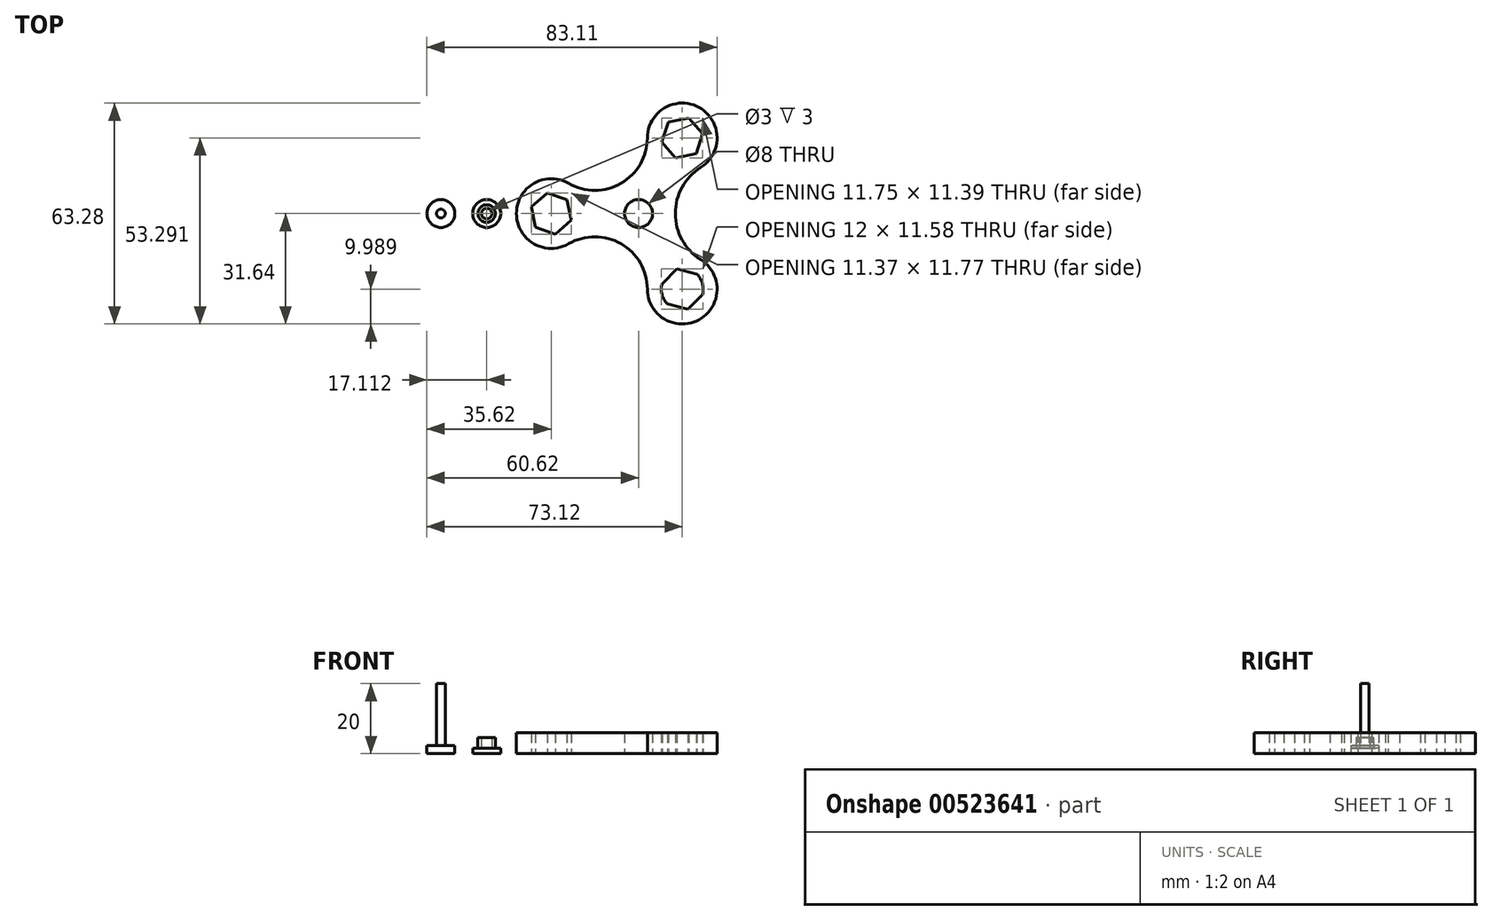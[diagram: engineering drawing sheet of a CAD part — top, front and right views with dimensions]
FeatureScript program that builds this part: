
annotation { "Feature Type Name" : "Feature", "Feature Type Description" : "" }
export const myFeature = defineFeature(function(context is Context, id is Id, definition is map)
    precondition{}
    {
        {
            var Q0;
            Q0=qCreatedBy(makeId("Top.planeOp"),FACE);
            var sketch = newSketch(context, id + "F0", { "sketchPlane" : qUnion([Q0])});
            skCircle(sketch, "E0", {"center": v(0, 0) * mm, "radius": 25 * mm});
            skCircle(sketch, "E1", {"center": v(-25, 0) * mm, "radius": 9.99 * mm});
            skCircle(sketch, "E2.2.1", {"center": v(12.5, -21.65) * mm, "radius": 9.99 * mm});
            skCircle(sketch, "E2.4.1", {"center": v(12.5, 21.65) * mm, "radius": 9.99 * mm});
            skCircle(sketch, "E3.cCircle", {"center": v(12.5, -21.65) * mm, "radius": 6 * mm, "construction": true});
            skLineSegment(sketch, "E3.0", {"start": v(8.28, -25.91) * mm, "end": v(6.7, -20.12) * mm});
            skLineSegment(sketch, "E3.1", {"start": v(6.7, -20.12) * mm, "end": v(10.92, -15.86) * mm});
            skLineSegment(sketch, "E3.2", {"start": v(10.92, -15.86) * mm, "end": v(16.72, -17.4) * mm});
            skLineSegment(sketch, "E3.3", {"start": v(16.72, -17.4) * mm, "end": v(18.3, -23.18) * mm});
            skLineSegment(sketch, "E3.4", {"start": v(18.3, -23.18) * mm, "end": v(14.08, -27.44) * mm});
            skLineSegment(sketch, "E3.5", {"start": v(14.08, -27.44) * mm, "end": v(8.28, -25.91) * mm});
            skCircle(sketch, "E4", {"center": v(12.5, -21.65) * mm, "radius": 6 * mm});
            skCircle(sketch, "E5", {"center": v(12.5, 21.65) * mm, "radius": 6 * mm});
            skCircle(sketch, "E6", {"center": v(-25, 0) * mm, "radius": 6 * mm});
            skCircle(sketch, "E7.cCircle", {"center": v(-25, 0) * mm, "radius": 6 * mm, "construction": true});
            skLineSegment(sketch, "E7.0", {"start": v(-29.5, -3.96) * mm, "end": v(-30.68, 1.92) * mm});
            skLineSegment(sketch, "E7.1", {"start": v(-30.68, 1.92) * mm, "end": v(-26.18, 5.88) * mm});
            skLineSegment(sketch, "E7.2", {"start": v(-26.18, 5.88) * mm, "end": v(-20.5, 3.96) * mm});
            skLineSegment(sketch, "E7.3", {"start": v(-20.5, 3.96) * mm, "end": v(-19.32, -1.92) * mm});
            skLineSegment(sketch, "E7.4", {"start": v(-19.32, -1.92) * mm, "end": v(-23.82, -5.88) * mm});
            skLineSegment(sketch, "E7.5", {"start": v(-23.82, -5.88) * mm, "end": v(-29.5, -3.96) * mm});
            skCircle(sketch, "E8.cCircle", {"center": v(12.5, 21.65) * mm, "radius": 6 * mm, "construction": true});
            skLineSegment(sketch, "E8.0", {"start": v(6.62, 20.44) * mm, "end": v(8.52, 26.14) * mm});
            skLineSegment(sketch, "E8.1", {"start": v(8.52, 26.14) * mm, "end": v(14.4, 27.34) * mm});
            skLineSegment(sketch, "E8.2", {"start": v(14.4, 27.34) * mm, "end": v(18.38, 22.86) * mm});
            skLineSegment(sketch, "E8.3", {"start": v(18.38, 22.86) * mm, "end": v(16.48, 17.16) * mm});
            skLineSegment(sketch, "E8.4", {"start": v(16.48, 17.16) * mm, "end": v(10.6, 15.96) * mm});
            skLineSegment(sketch, "E8.5", {"start": v(10.6, 15.96) * mm, "end": v(6.62, 20.44) * mm});
            skArc(sketch, "E9", {"start": v(2.15, -24.9) * mm, "mid": v(-5, -8.65) * mm, "end": v(-22.65, -10.59) * mm});
            skArc(sketch, "E10", {"start": v(-22.65, 10.59) * mm, "mid": v(-5, 8.65) * mm, "end": v(2.15, 24.9) * mm});
            skArc(sketch, "E11", {"start": v(20.38, 14.49) * mm, "mid": v(10.51, 0) * mm, "end": v(20.38, -14.49) * mm});
            skPoint(sketch, "E2.3.1.center.orphan", {"position": v(25, 0) * mm});
            skCircle(sketch, "E12", {"center": v(0, 0) * mm, "radius": 4 * mm});
            skSolve(sketch);
        }
        {
            var Q0;
            {var subQ1=sQuery(id+"F0.wireOp",EDGE,"E1");var subQ8=sQuery(id+"F0.wireOp",EDGE,"E10");var subQ10=makeQuery(id+"F0.imprint","INTERSECT",VERTEX,{"derivedFrom":[subQ1,subQ8]});Q0=makeQuery(id+"F0.imprint","IMPRINT",FACE,{"disambiguationData":[TD([[makeQuery(id+"F0.imprint","IMPRINT",EDGE,{"disambiguationData":[TD([[subQ10,1.0]])],"derivedFrom":subQ1}),-1.0]])]});}
            var Q1;
            {var subQ0=sQuery(id+"F0.wireOp",EDGE,"E1");var subQ3=sQuery(id+"F0.wireOp",EDGE,"E0");var subQ4=makeQuery(id+"F0.imprint","INTERSECT",VERTEX,{"disambiguationData":[OD(0.0)],"derivedFrom":[subQ0,subQ3]});Q1=makeQuery(id+"F0.imprint","IMPRINT",FACE,{"disambiguationData":[TD([[makeQuery(id+"F0.imprint","IMPRINT",EDGE,{"disambiguationData":[TD([[subQ4,1.0]])],"derivedFrom":subQ0}),1.0]])]});}
            var Q2;
            {var subQ0=sQuery(id+"F0.wireOp",EDGE,"E0");var subQ1=sQuery(id+"F0.wireOp",EDGE,"E1");var subQ9=makeQuery(id+"F0.imprint","INTERSECT",VERTEX,{"disambiguationData":[OD(0.0)],"derivedFrom":[subQ1,subQ0]});Q2=makeQuery(id+"F0.imprint","IMPRINT",FACE,{"disambiguationData":[TD([[makeQuery(id+"F0.imprint","IMPRINT",EDGE,{"disambiguationData":[TD([[subQ9,-1.0]])],"derivedFrom":subQ1}),1.0]])]});}
            var Q3;
            {var subQ0=sQuery(id+"F0.wireOp",EDGE,"E7.1");Q3=makeQuery(id+"F0.imprint","IMPRINT",FACE,{"disambiguationData":[TD([[makeQuery(id+"F0.imprint","IMPRINT",EDGE,{"derivedFrom":subQ0}),1.0]])]});}
            var Q4;
            {var subQ0=sQuery(id+"F0.wireOp",EDGE,"E7.0");Q4=makeQuery(id+"F0.imprint","IMPRINT",FACE,{"disambiguationData":[TD([[makeQuery(id+"F0.imprint","IMPRINT",EDGE,{"derivedFrom":subQ0}),1.0]])]});}
            var Q5;
            {var subQ0=sQuery(id+"F0.wireOp",EDGE,"E7.5");var subQ1=sQuery(id+"F0.wireOp",EDGE,"E0");var subQ2=makeQuery(id+"F0.imprint","INTERSECT",VERTEX,{"derivedFrom":[subQ1,subQ0]});Q5=makeQuery(id+"F0.imprint","IMPRINT",FACE,{"disambiguationData":[TD([[makeQuery(id+"F0.imprint","IMPRINT",EDGE,{"disambiguationData":[TD([[subQ2,-1.0]])],"derivedFrom":subQ1}),-1.0]])]});}
            var Q6;
            {var subQ0=sQuery(id+"F0.wireOp",EDGE,"E7.4");Q6=makeQuery(id+"F0.imprint","IMPRINT",FACE,{"disambiguationData":[TD([[makeQuery(id+"F0.imprint","IMPRINT",EDGE,{"derivedFrom":subQ0}),1.0]])]});}
            var Q7;
            {var subQ0=sQuery(id+"F0.wireOp",EDGE,"E7.3");Q7=makeQuery(id+"F0.imprint","IMPRINT",FACE,{"disambiguationData":[TD([[makeQuery(id+"F0.imprint","IMPRINT",EDGE,{"derivedFrom":subQ0}),1.0]])]});}
            var Q8;
            {var subQ0=sQuery(id+"F0.wireOp",EDGE,"E6");var subQ1=sQuery(id+"F0.wireOp",EDGE,"E0");var subQ2=makeQuery(id+"F0.imprint","INTERSECT",VERTEX,{"disambiguationData":[OD(0.0)],"derivedFrom":[subQ1,subQ0]});Q8=makeQuery(id+"F0.imprint","IMPRINT",FACE,{"disambiguationData":[TD([[makeQuery(id+"F0.imprint","IMPRINT",EDGE,{"disambiguationData":[TD([[subQ2,-1.0]])],"derivedFrom":subQ1}),1.0]])]});}
            var Q9;
            {var subQ0=sQuery(id+"F0.wireOp",EDGE,"E0");var subQ1=sQuery(id+"F0.wireOp",EDGE,"E2.2.1");var subQ11=makeQuery(id+"F0.imprint","INTERSECT",VERTEX,{"disambiguationData":[OD(0.0)],"derivedFrom":[subQ1,subQ0]});Q9=makeQuery(id+"F0.imprint","IMPRINT",FACE,{"disambiguationData":[TD([[makeQuery(id+"F0.imprint","IMPRINT",EDGE,{"disambiguationData":[TD([[subQ11,1.0]])],"derivedFrom":subQ1}),1.0]])]});}
            var Q10;
            {var subQ3=sQuery(id+"F0.wireOp",EDGE,"E0");var subQ5=sQuery(id+"F0.wireOp",EDGE,"E2.2.1");var subQ6=makeQuery(id+"F0.imprint","INTERSECT",VERTEX,{"disambiguationData":[OD(0.0)],"derivedFrom":[subQ5,subQ3]});Q10=makeQuery(id+"F0.imprint","IMPRINT",FACE,{"disambiguationData":[TD([[makeQuery(id+"F0.imprint","IMPRINT",EDGE,{"disambiguationData":[TD([[subQ6,-1.0]])],"derivedFrom":subQ5}),1.0]])]});}
            var Q11;
            {var subQ0=sQuery(id+"F0.wireOp",EDGE,"E3.4");Q11=makeQuery(id+"F0.imprint","IMPRINT",FACE,{"disambiguationData":[TD([[makeQuery(id+"F0.imprint","IMPRINT",EDGE,{"derivedFrom":subQ0}),1.0]])]});}
            var Q12;
            {var subQ0=sQuery(id+"F0.wireOp",EDGE,"E3.5");Q12=makeQuery(id+"F0.imprint","IMPRINT",FACE,{"disambiguationData":[TD([[makeQuery(id+"F0.imprint","IMPRINT",EDGE,{"derivedFrom":subQ0}),1.0]])]});}
            var Q13;
            {var subQ0=sQuery(id+"F0.wireOp",EDGE,"E4");var subQ1=sQuery(id+"F0.wireOp",EDGE,"E0");var subQ2=makeQuery(id+"F0.imprint","INTERSECT",VERTEX,{"disambiguationData":[OD(1.0)],"derivedFrom":[subQ1,subQ0]});Q13=makeQuery(id+"F0.imprint","IMPRINT",FACE,{"disambiguationData":[TD([[makeQuery(id+"F0.imprint","IMPRINT",EDGE,{"disambiguationData":[TD([[subQ2,-1.0]])],"derivedFrom":subQ1}),1.0]])]});}
            var Q14;
            {var subQ0=sQuery(id+"F0.wireOp",EDGE,"E4");var subQ1=sQuery(id+"F0.wireOp",EDGE,"E0");var subQ2=makeQuery(id+"F0.imprint","INTERSECT",VERTEX,{"disambiguationData":[OD(1.0)],"derivedFrom":[subQ1,subQ0]});Q14=makeQuery(id+"F0.imprint","IMPRINT",FACE,{"disambiguationData":[TD([[makeQuery(id+"F0.imprint","IMPRINT",EDGE,{"disambiguationData":[TD([[subQ2,-1.0]])],"derivedFrom":subQ1}),-1.0]])]});}
            var Q15;
            {var subQ0=sQuery(id+"F0.wireOp",EDGE,"E3.1");Q15=makeQuery(id+"F0.imprint","IMPRINT",FACE,{"disambiguationData":[TD([[makeQuery(id+"F0.imprint","IMPRINT",EDGE,{"derivedFrom":subQ0}),1.0]])]});}
            var Q16;
            {var subQ0=sQuery(id+"F0.wireOp",EDGE,"E3.2");Q16=makeQuery(id+"F0.imprint","IMPRINT",FACE,{"disambiguationData":[TD([[makeQuery(id+"F0.imprint","IMPRINT",EDGE,{"derivedFrom":subQ0}),1.0]])]});}
            var Q17;
            {var subQ0=sQuery(id+"F0.wireOp",EDGE,"E4");var subQ1=sQuery(id+"F0.wireOp",EDGE,"E0");var subQ2=makeQuery(id+"F0.imprint","INTERSECT",VERTEX,{"disambiguationData":[OD(0.0)],"derivedFrom":[subQ1,subQ0]});Q17=makeQuery(id+"F0.imprint","IMPRINT",FACE,{"disambiguationData":[TD([[makeQuery(id+"F0.imprint","IMPRINT",EDGE,{"disambiguationData":[TD([[subQ2,1.0]])],"derivedFrom":subQ1}),-1.0]])]});}
            var Q18;
            {var subQ0=sQuery(id+"F0.wireOp",EDGE,"E4");var subQ1=sQuery(id+"F0.wireOp",EDGE,"E0");var subQ2=makeQuery(id+"F0.imprint","INTERSECT",VERTEX,{"disambiguationData":[OD(0.0)],"derivedFrom":[subQ1,subQ0]});Q18=makeQuery(id+"F0.imprint","IMPRINT",FACE,{"disambiguationData":[TD([[makeQuery(id+"F0.imprint","IMPRINT",EDGE,{"disambiguationData":[TD([[subQ2,1.0]])],"derivedFrom":subQ1}),1.0]])]});}
            var Q19;
            {var subQ0=sQuery(id+"F0.wireOp",EDGE,"E0");var subQ1=sQuery(id+"F0.wireOp",EDGE,"E2.4.1");var subQ2=makeQuery(id+"F0.imprint","INTERSECT",VERTEX,{"disambiguationData":[OD(0.0)],"derivedFrom":[subQ1,subQ0]});Q19=makeQuery(id+"F0.imprint","IMPRINT",FACE,{"disambiguationData":[TD([[makeQuery(id+"F0.imprint","IMPRINT",EDGE,{"disambiguationData":[TD([[subQ2,1.0]])],"derivedFrom":subQ1}),1.0]])]});}
            var Q20;
            {var subQ0=sQuery(id+"F0.wireOp",EDGE,"E0");var subQ1=sQuery(id+"F0.wireOp",EDGE,"E2.4.1");var subQ10=makeQuery(id+"F0.imprint","INTERSECT",VERTEX,{"disambiguationData":[OD(0.0)],"derivedFrom":[subQ1,subQ0]});Q20=makeQuery(id+"F0.imprint","IMPRINT",FACE,{"disambiguationData":[TD([[makeQuery(id+"F0.imprint","IMPRINT",EDGE,{"disambiguationData":[TD([[subQ10,-1.0]])],"derivedFrom":subQ1}),1.0]])]});}
            var Q21;
            {var subQ0=sQuery(id+"F0.wireOp",EDGE,"E8.5");Q21=makeQuery(id+"F0.imprint","IMPRINT",FACE,{"disambiguationData":[TD([[makeQuery(id+"F0.imprint","IMPRINT",EDGE,{"derivedFrom":subQ0}),1.0]])]});}
            var Q22;
            {var subQ0=sQuery(id+"F0.wireOp",EDGE,"E8.0");var subQ1=sQuery(id+"F0.wireOp",EDGE,"E0");var subQ2=makeQuery(id+"F0.imprint","INTERSECT",VERTEX,{"derivedFrom":[subQ1,subQ0]});Q22=makeQuery(id+"F0.imprint","IMPRINT",FACE,{"disambiguationData":[TD([[makeQuery(id+"F0.imprint","IMPRINT",EDGE,{"disambiguationData":[TD([[subQ2,-1.0]])],"derivedFrom":subQ1}),1.0]])]});}
            var Q23;
            {var subQ0=sQuery(id+"F0.wireOp",EDGE,"E8.0");var subQ1=sQuery(id+"F0.wireOp",EDGE,"E0");var subQ2=makeQuery(id+"F0.imprint","INTERSECT",VERTEX,{"derivedFrom":[subQ1,subQ0]});Q23=makeQuery(id+"F0.imprint","IMPRINT",FACE,{"disambiguationData":[TD([[makeQuery(id+"F0.imprint","IMPRINT",EDGE,{"disambiguationData":[TD([[subQ2,-1.0]])],"derivedFrom":subQ1}),-1.0]])]});}
            var Q24;
            {var subQ0=sQuery(id+"F0.wireOp",EDGE,"E8.1");Q24=makeQuery(id+"F0.imprint","IMPRINT",FACE,{"disambiguationData":[TD([[makeQuery(id+"F0.imprint","IMPRINT",EDGE,{"derivedFrom":subQ0}),1.0]])]});}
            var Q25;
            {var subQ0=sQuery(id+"F0.wireOp",EDGE,"E8.2");Q25=makeQuery(id+"F0.imprint","IMPRINT",FACE,{"disambiguationData":[TD([[makeQuery(id+"F0.imprint","IMPRINT",EDGE,{"derivedFrom":subQ0}),1.0]])]});}
            var Q26;
            {var subQ0=sQuery(id+"F0.wireOp",EDGE,"E5");var subQ1=sQuery(id+"F0.wireOp",EDGE,"E0");var subQ2=makeQuery(id+"F0.imprint","INTERSECT",VERTEX,{"disambiguationData":[OD(0.0)],"derivedFrom":[subQ1,subQ0]});Q26=makeQuery(id+"F0.imprint","IMPRINT",FACE,{"disambiguationData":[TD([[makeQuery(id+"F0.imprint","IMPRINT",EDGE,{"disambiguationData":[TD([[subQ2,-1.0]])],"derivedFrom":subQ1}),-1.0]])]});}
            var Q27;
            {var subQ0=sQuery(id+"F0.wireOp",EDGE,"E5");var subQ1=sQuery(id+"F0.wireOp",EDGE,"E0");var subQ2=makeQuery(id+"F0.imprint","INTERSECT",VERTEX,{"disambiguationData":[OD(0.0)],"derivedFrom":[subQ1,subQ0]});Q27=makeQuery(id+"F0.imprint","IMPRINT",FACE,{"disambiguationData":[TD([[makeQuery(id+"F0.imprint","IMPRINT",EDGE,{"disambiguationData":[TD([[subQ2,-1.0]])],"derivedFrom":subQ1}),1.0]])]});}
            var Q28;
            {var subQ0=sQuery(id+"F0.wireOp",EDGE,"E8.4");Q28=makeQuery(id+"F0.imprint","IMPRINT",FACE,{"disambiguationData":[TD([[makeQuery(id+"F0.imprint","IMPRINT",EDGE,{"derivedFrom":subQ0}),1.0]])]});}
            var Q29;
            {var subQ0=sQuery(id+"F0.wireOp",EDGE,"E6");var subQ1=sQuery(id+"F0.wireOp",EDGE,"E0");var subQ2=makeQuery(id+"F0.imprint","INTERSECT",VERTEX,{"disambiguationData":[OD(0.0)],"derivedFrom":[subQ1,subQ0]});Q29=makeQuery(id+"F0.imprint","IMPRINT",FACE,{"disambiguationData":[TD([[makeQuery(id+"F0.imprint","IMPRINT",EDGE,{"disambiguationData":[TD([[subQ2,-1.0]])],"derivedFrom":subQ1}),-1.0]])]});}
            var Q30;
            {var subQ0=sQuery(id+"F0.wireOp",EDGE,"E7.5");var subQ1=sQuery(id+"F0.wireOp",EDGE,"E0");var subQ2=makeQuery(id+"F0.imprint","INTERSECT",VERTEX,{"derivedFrom":[subQ1,subQ0]});Q30=makeQuery(id+"F0.imprint","IMPRINT",FACE,{"disambiguationData":[TD([[makeQuery(id+"F0.imprint","IMPRINT",EDGE,{"disambiguationData":[TD([[subQ2,-1.0]])],"derivedFrom":subQ1}),1.0]])]});}
            extrude(context, id + "F1", {"entities" : qUnion([Q0, Q1, Q2, Q3, Q4, Q5, Q6, Q7, Q8, Q9, Q10, Q11, Q12, Q13, Q14, Q15, Q16, Q17, Q18, Q19, Q20, Q21, Q22, Q23, Q24, Q25, Q26, Q27, Q28, Q29, Q30]), "depth" : 6 * mm, "offsetDistance" : 25 * mm});
        }
        {
            var Q0;
            Q0=qCreatedBy(makeId("Top.planeOp"),FACE);
            var sketch = newSketch(context, id + "F2", { "sketchPlane" : qUnion([Q0])});
            skCircle(sketch, "E13", {"center": v(-43.5, 0) * mm, "radius": 4 * mm});
            skCircle(sketch, "E14", {"center": v(-56.62, 0) * mm, "radius": 4 * mm});
            skCircle(sketch, "E15", {"center": v(-56.62, 0) * mm, "radius": 1.25 * mm});
            skCircle(sketch, "E16", {"center": v(-43.5, 0) * mm, "radius": 1.5 * mm});
            skCircle(sketch, "E17", {"center": v(-43.5, 0) * mm, "radius": 2.5 * mm});
            skSolve(sketch);
        }
        {
            var Q0;
            Q0=makeQuery(id+"F2.imprint","IMPRINT",FACE,{"disambiguationData":[TD([[makeQuery(id+"F2.imprint","IMPRINT",EDGE,{"derivedFrom":sQuery(id+"F2.wireOp",EDGE,"E14")}),1.0]])]});
            extrude(context, id + "F3", {"entities" : qUnion([Q0]), "depth" : 2.25 * mm, "offsetDistance" : 25 * mm});
        }
        {
            var Q0;
            Q0=makeQuery(id+"F2.imprint","IMPRINT",FACE,{"disambiguationData":[TD([[makeQuery(id+"F2.imprint","IMPRINT",EDGE,{"derivedFrom":sQuery(id+"F2.wireOp",EDGE,"E15")}),1.0]])]});
            extrude(context, id + "F4", {"entities" : qUnion([Q0]), "operationType" : NewBodyOperationType.ADD, "depth" : 20 * mm, "offsetDistance" : 25 * mm});
        }
        {
            var Q0;
            Q0=makeQuery(id+"F2.imprint","IMPRINT",FACE,{"disambiguationData":[TD([[makeQuery(id+"F2.imprint","IMPRINT",EDGE,{"derivedFrom":sQuery(id+"F2.wireOp",EDGE,"E13")}),1.0]])]});
            extrude(context, id + "F5", {"entities" : qUnion([Q0]), "depth" : 1.5 * mm, "offsetDistance" : 25 * mm});
        }
        {
            var Q0;
            Q0=makeQuery(id+"F2.imprint","IMPRINT",FACE,{"disambiguationData":[TD([[makeQuery(id+"F2.imprint","IMPRINT",EDGE,{"derivedFrom":sQuery(id+"F2.wireOp",EDGE,"E16")}),-1.0]])]});
            extrude(context, id + "F6", {"entities" : qUnion([Q0]), "operationType" : NewBodyOperationType.ADD, "depth" : 4.5 * mm, "offsetDistance" : 25 * mm});
        }
        {
            var Q0;
            Q0=makeQuery(id+"F2.imprint","IMPRINT",FACE,{"disambiguationData":[TD([[makeQuery(id+"F2.imprint","IMPRINT",EDGE,{"derivedFrom":sQuery(id+"F2.wireOp",EDGE,"E16")}),1.0]])]});
            extrude(context, id + "F7", {"entities" : qUnion([Q0]), "operationType" : NewBodyOperationType.ADD, "depth" : 1.5 * mm, "offsetDistance" : 25 * mm});
        }
    });
